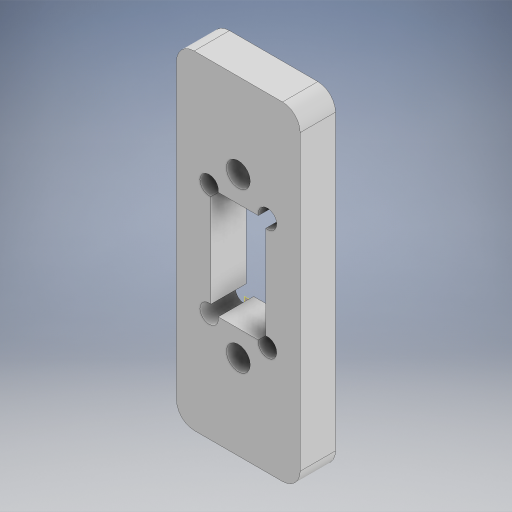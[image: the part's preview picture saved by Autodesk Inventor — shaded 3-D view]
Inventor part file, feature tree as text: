
AUTODESK INVENTOR PART (.ipt)
format: ipt  version: 2024 (Build 280153000, 153)  size: 332,800 bytes
history: native  units: mm
features: other x5, sketch x3, reference x3, extrude x2, projected_geometry x2, fillet x1, hole x1
ambient origin geometry x8: Origin, YZ Plane, XZ Plane, XY Plane, X Axis, Y Axis, Z Axis, Center Point
bodies: Body1 (feature_tree)
feature tree (17):
  other  "솔리드1"
  other  "작업 평면1"
  extrude  "돌출1"  Depth=0.3mm
  fillet  "모깎기1"  Radius=1.5mm
  extrude  "돌출2"  Depth=1.5mm
  hole  "구멍1"  [1 undecoded]
  sketch  "스케치1"
  reference  "참조1"
  reference  "참조2"
  reference  "참조3"
  sketch  "스케치2"
  projected_geometry  "투영된 루프1"
  sketch  "스케치3"
  projected_geometry  "투영된 루프2"
  other  "<userpath>\Desktop\ZIG\조립품1.iam"
  other  "조립품1.iam"
  other  "body_front_front:1"
note: 1 required parameter value undecoded (feature->parameter linkage not recoverable at this tier; creation-order binding heuristic only, values carry confidence <= 0.55)
